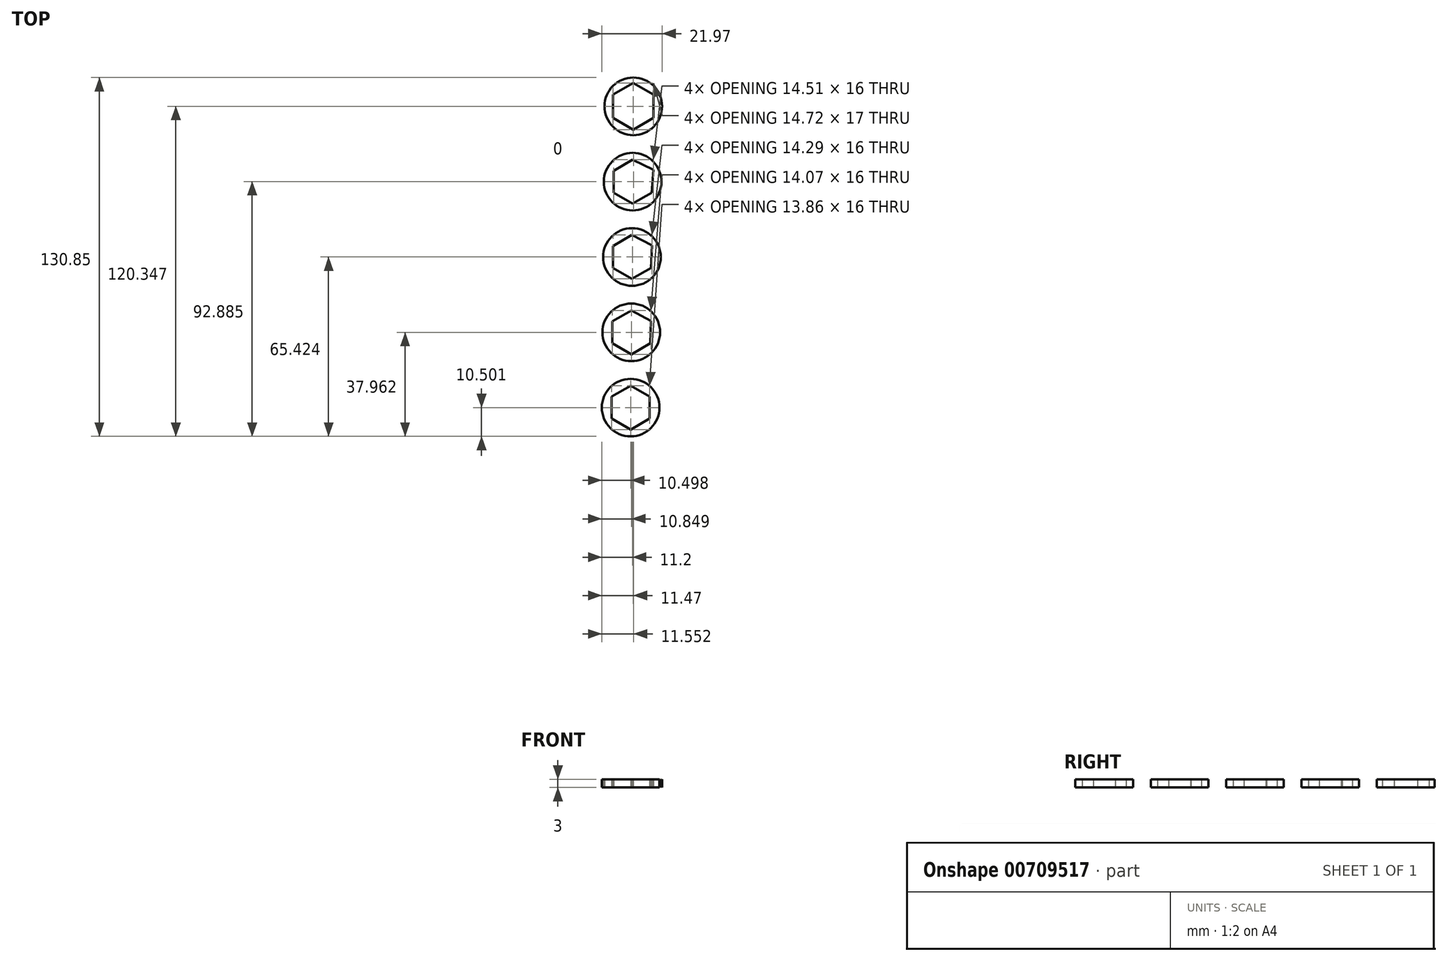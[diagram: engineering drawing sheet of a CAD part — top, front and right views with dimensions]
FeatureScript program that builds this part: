
annotation { "Feature Type Name" : "Feature", "Feature Type Description" : "" }
export const myFeature = defineFeature(function(context is Context, id is Id, definition is map)
    precondition{}
    {
        {
            var Q0;
            Q0=qCreatedBy(makeId("Top.planeOp"),FACE);
            var sketch = newSketch(context, id + "F0", { "sketchPlane" : qUnion([Q0])});
            skCircle(sketch, "E0.cCircle", {"center": v(0, 53.89) * mm, "radius": 8.5 * mm, "construction": true});
            skLineSegment(sketch, "E0.0", {"start": v(0, 62.39) * mm, "end": v(7.36, 58.14) * mm});
            skLineSegment(sketch, "E0.1", {"start": v(7.36, 58.14) * mm, "end": v(7.36, 49.64) * mm});
            skLineSegment(sketch, "E0.2", {"start": v(7.36, 49.64) * mm, "end": v(0, 45.39) * mm});
            skLineSegment(sketch, "E0.3", {"start": v(0, 45.39) * mm, "end": v(-7.36, 49.64) * mm});
            skLineSegment(sketch, "E0.4", {"start": v(-7.36, 49.64) * mm, "end": v(-7.36, 58.14) * mm});
            skLineSegment(sketch, "E0.5", {"start": v(-7.36, 58.14) * mm, "end": v(0, 62.39) * mm});
            skCircle(sketch, "E1.1.0.0", {"center": v(-0.24, 26.43) * mm, "radius": 8 * mm, "construction": true});
            skLineSegment(sketch, "E1.1.0.1", {"start": v(-0.24, 34.43) * mm, "end": v(7.33, 30.8) * mm});
            skLineSegment(sketch, "E1.1.0.2", {"start": v(7.33, 30.8) * mm, "end": v(6.69, 22.43) * mm});
            skLineSegment(sketch, "E1.1.0.3", {"start": v(6.69, 22.43) * mm, "end": v(-0.24, 18.43) * mm});
            skLineSegment(sketch, "E1.1.0.4", {"start": v(-0.24, 18.43) * mm, "end": v(-7.17, 22.43) * mm});
            skLineSegment(sketch, "E1.1.0.5", {"start": v(-7.17, 22.43) * mm, "end": v(-7.17, 30.43) * mm});
            skLineSegment(sketch, "E1.1.0.6", {"start": v(-7.17, 30.43) * mm, "end": v(-0.24, 34.43) * mm});
            skCircle(sketch, "E1.2.0.0", {"center": v(-0.49, -1.04) * mm, "radius": 8 * mm, "construction": true});
            skLineSegment(sketch, "E1.2.0.1", {"start": v(-0.49, 6.96) * mm, "end": v(6.88, 3.21) * mm});
            skLineSegment(sketch, "E1.2.0.2", {"start": v(6.88, 3.21) * mm, "end": v(6.44, -5.04) * mm});
            skLineSegment(sketch, "E1.2.0.3", {"start": v(6.44, -5.04) * mm, "end": v(-0.49, -9.04) * mm});
            skLineSegment(sketch, "E1.2.0.4", {"start": v(-0.49, -9.04) * mm, "end": v(-7.41, -5.04) * mm});
            skLineSegment(sketch, "E1.2.0.5", {"start": v(-7.41, -5.04) * mm, "end": v(-7.41, 2.96) * mm});
            skLineSegment(sketch, "E1.2.0.6", {"start": v(-7.41, 2.96) * mm, "end": v(-0.49, 6.96) * mm});
            skCircle(sketch, "E1.3.0.0", {"center": v(-0.73, -28.5) * mm, "radius": 8 * mm, "construction": true});
            skLineSegment(sketch, "E1.3.0.1", {"start": v(-0.73, -20.5) * mm, "end": v(6.42, -24.37) * mm});
            skLineSegment(sketch, "E1.3.0.2", {"start": v(6.42, -24.37) * mm, "end": v(6.2, -32.5) * mm});
            skLineSegment(sketch, "E1.3.0.3", {"start": v(6.2, -32.5) * mm, "end": v(-0.73, -36.5) * mm});
            skLineSegment(sketch, "E1.3.0.4", {"start": v(-0.73, -36.5) * mm, "end": v(-7.66, -32.5) * mm});
            skLineSegment(sketch, "E1.3.0.5", {"start": v(-7.66, -32.5) * mm, "end": v(-7.66, -24.5) * mm});
            skLineSegment(sketch, "E1.3.0.6", {"start": v(-7.66, -24.5) * mm, "end": v(-0.73, -20.5) * mm});
            skCircle(sketch, "E1.4.0.0", {"center": v(-0.97, -55.96) * mm, "radius": 8 * mm, "construction": true});
            skLineSegment(sketch, "E1.4.0.1", {"start": v(-0.97, -47.96) * mm, "end": v(5.96, -51.96) * mm});
            skLineSegment(sketch, "E1.4.0.2", {"start": v(5.96, -51.96) * mm, "end": v(5.96, -59.96) * mm});
            skLineSegment(sketch, "E1.4.0.3", {"start": v(5.96, -59.96) * mm, "end": v(-0.97, -63.96) * mm});
            skLineSegment(sketch, "E1.4.0.4", {"start": v(-0.97, -63.96) * mm, "end": v(-7.9, -59.96) * mm});
            skLineSegment(sketch, "E1.4.0.5", {"start": v(-7.9, -59.96) * mm, "end": v(-7.9, -51.96) * mm});
            skLineSegment(sketch, "E1.4.0.6", {"start": v(-7.9, -51.96) * mm, "end": v(-0.97, -47.96) * mm});
            skCircle(sketch, "E2", {"center": v(0, 53.89) * mm, "radius": 10.5 * mm});
            skCircle(sketch, "E3", {"center": v(-0.24, 26.43) * mm, "radius": 10.5 * mm});
            skCircle(sketch, "E4", {"center": v(-0.49, -1.04) * mm, "radius": 10.5 * mm});
            skCircle(sketch, "E5", {"center": v(-0.73, -28.5) * mm, "radius": 10.5 * mm});
            skCircle(sketch, "E6", {"center": v(-0.97, -55.96) * mm, "radius": 10.5 * mm});
            skSolve(sketch);
        }
        {
            var Q0;
            Q0=makeQuery(id+"F0.imprint","IMPRINT",FACE,{"disambiguationData":[TD([[makeQuery(id+"F0.imprint","IMPRINT",EDGE,{"derivedFrom":sQuery(id+"F0.wireOp",EDGE,"E0.0")}),1.0]])]});
            var Q1;
            Q1=makeQuery(id+"F0.imprint","IMPRINT",FACE,{"disambiguationData":[TD([[makeQuery(id+"F0.imprint","IMPRINT",EDGE,{"derivedFrom":sQuery(id+"F0.wireOp",EDGE,"E1.1.0.1")}),1.0]])]});
            var Q2;
            Q2=makeQuery(id+"F0.imprint","IMPRINT",FACE,{"disambiguationData":[TD([[makeQuery(id+"F0.imprint","IMPRINT",EDGE,{"derivedFrom":sQuery(id+"F0.wireOp",EDGE,"E1.2.0.1")}),1.0]])]});
            var Q3;
            Q3=makeQuery(id+"F0.imprint","IMPRINT",FACE,{"disambiguationData":[TD([[makeQuery(id+"F0.imprint","IMPRINT",EDGE,{"derivedFrom":sQuery(id+"F0.wireOp",EDGE,"E1.3.0.1")}),1.0]])]});
            var Q4;
            Q4=makeQuery(id+"F0.imprint","IMPRINT",FACE,{"disambiguationData":[TD([[makeQuery(id+"F0.imprint","IMPRINT",EDGE,{"derivedFrom":sQuery(id+"F0.wireOp",EDGE,"E1.4.0.1")}),1.0]])]});
            extrude(context, id + "F1", {"entities" : qUnion([Q0, Q1, Q2, Q3, Q4]), "depth" : 3 * mm, "offsetDistance" : 25 * mm});
        }
    });
